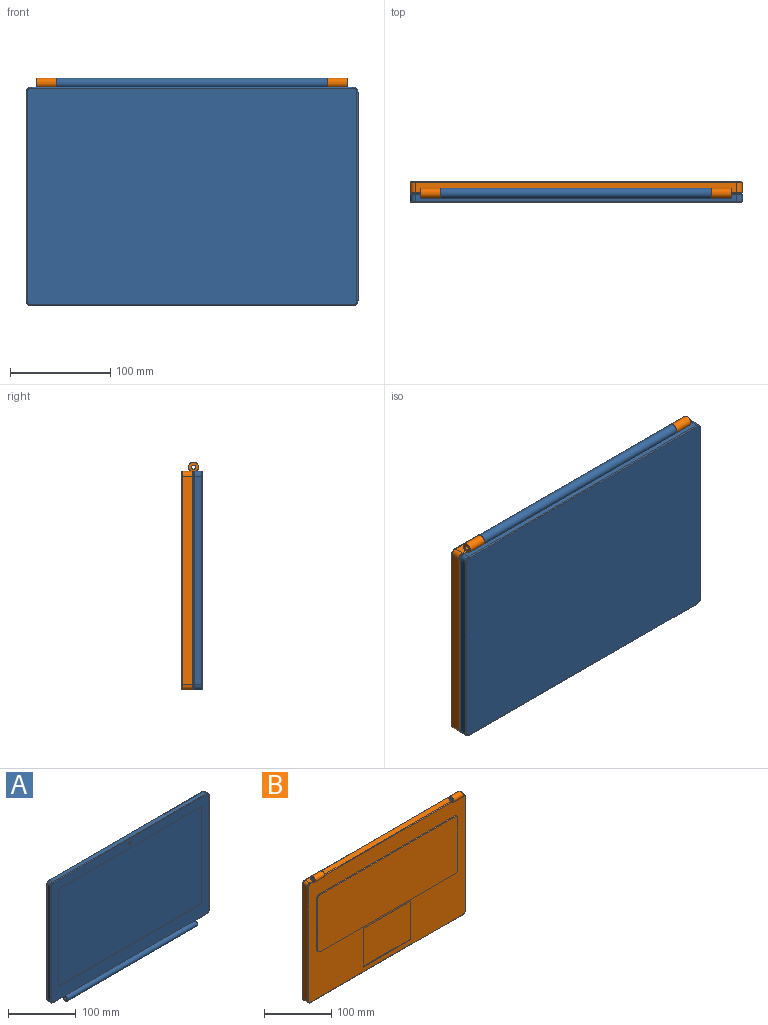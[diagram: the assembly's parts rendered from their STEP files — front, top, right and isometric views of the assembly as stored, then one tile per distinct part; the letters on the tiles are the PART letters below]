
ASSEMBLY  parts=2 mates=1
PART A: 38 faces, bbox 331.8x14x227.4 mm
  f0: plane 208x7mm, normal (-1,0,0), area 1456mm2, adj f17,f20,f23,f30
  f1: plane 321x7mm, normal (0,0,-1), area 1705mm2, adj f13,f14,f15,f17,f18,f21,f29,f34
  f2: plane 208x7mm, normal (1,0,0), area 1456mm2, adj f18,f19,f27,f37
  f3: plane 321x7mm, normal (0,0,1), area 2247mm2, adj f19,f20,f25,f33
  f4: plane 329x216mm, normal (0,-1,0), area 18398mm2, adj f6,f7,f8,f9,f11,f13,f21,f22
  f5: plane 329x216mm, normal (0,1,0), area 71050.3mm2, adj f30,f31,f32,f33,f34,f35,f36,f37
  f6: plane 176x1mm, normal (1,0,0), area 176mm2, adj f4,f7,f9,f10
  f7: plane 299x1mm, normal (0,0,1), area 299mm2, adj f4,f6,f8,f10
  f8: plane 176x1mm, normal (-1,0,0), area 176mm2, adj f4,f7,f9,f10
  f9: plane 299x1mm, normal (0,0,-1), area 299mm2, adj f4,f6,f8,f10
  f10: plane 299x176mm, normal (0,-1,0), area 52624mm2, adj f6,f7,f8,f9
  f11: cylinder r=3mm len=6mm, axis (0,-1,0), area 37.7mm2, adj f4,f12
  f12: plane 6x6mm, normal (0,-1,0), area 28.3mm2, adj f11
  f13: cylinder r=5mm len=271mm, axis (-1,0,0), area 7641.8mm2, adj f1,f4,f14,f15
  f14: plane 10x10mm, normal (1,0,0), area 64.1mm2, adj f1,f13,f16,f29
  f15: plane 10x10mm, normal (-1,0,0), area 64.1mm2, adj f1,f13,f16,f21
  f16: cylinder r=2mm len=271mm, axis (-1,0,0), area 3405.5mm2, adj f14,f15
  f17: cylinder r=5mm len=7mm, axis (0,1,0), area 55mm2, adj f0,f1,f22,f32
  f18: cylinder r=5mm len=7mm, axis (0,-1,0), area 55mm2, adj f1,f2,f28,f36
  f19: cylinder r=5mm len=7mm, axis (0,1,0), area 55mm2, adj f2,f3,f26,f35
  f20: cylinder r=5mm len=7mm, axis (0,-1,0), area 55mm2, adj f0,f3,f24,f31
  f21: cylinder r=1mm len=25mm, axis (-1,0,0), area 39.3mm2, adj f1,f4,f15,f22
  f22: torus R=4mm, axis (0,-1,0), area 11.4mm2, adj f4,f17,f21,f23
  f23: cylinder r=1mm len=208mm, axis (0,0,1), area 326.7mm2, adj f0,f4,f22,f24
  f24: torus R=4mm, axis (0,-1,0), area 11.4mm2, adj f4,f20,f23,f25
  f25: cylinder r=1mm len=321mm, axis (1,0,0), area 504.2mm2, adj f3,f4,f24,f26
  f26: torus R=4mm, axis (0,-1,0), area 11.4mm2, adj f4,f19,f25,f27
  f27: cylinder r=1mm len=208mm, axis (0,0,-1), area 326.7mm2, adj f2,f4,f26,f28
  f28: torus R=4mm, axis (0,-1,0), area 11.4mm2, adj f4,f18,f27,f29
  f29: cylinder r=1mm len=25mm, axis (-1,0,0), area 39.3mm2, adj f1,f4,f14,f28
  f30: cylinder r=1mm len=208mm, axis (0,0,-1), area 326.7mm2, adj f0,f5,f31,f32
  f31: torus R=4mm, axis (0,-1,0), area 11.4mm2, adj f5,f20,f30,f33
  f32: torus R=4mm, axis (0,-1,0), area 11.4mm2, adj f5,f17,f30,f34
  f33: cylinder r=1mm len=321mm, axis (-1,0,0), area 504.2mm2, adj f3,f5,f31,f35
  f34: cylinder r=1mm len=321mm, axis (1,0,0), area 504.2mm2, adj f1,f5,f32,f36
  f35: torus R=4mm, axis (0,-1,0), area 11.4mm2, adj f5,f19,f33,f37
  f36: torus R=4mm, axis (0,-1,0), area 11.4mm2, adj f5,f18,f34,f37
  f37: cylinder r=1mm len=208mm, axis (0,0,1), area 326.7mm2, adj f2,f5,f35,f36
PART B: 50 faces, bbox 331.8x17x227.4 mm
  f0: plane 321x10mm, normal (0,0,1), area 3130mm2, adj f20,f22,f23,f24,f26,f27,f30,f31
  f1: plane 329x216mm, normal (0,-1,0), area 33495.7mm2, adj f6,f7,f8,f9,f11,f12,f13,f14
  f2: plane 208x10mm, normal (-1,0,0), area 2080mm2, adj f28,f31,f36,f47
  f3: plane 321x10mm, normal (0,0,-1), area 3210mm2, adj f28,f29,f40,f46
  f4: plane 208x10mm, normal (1,0,0), area 2080mm2, adj f29,f30,f37,f42
  f5: plane 329x216mm, normal (0,1,0), area 71050.3mm2, adj f41,f42,f43,f44,f45,f46,f47,f48
  f6: plane 94x2mm, normal (-1,0,0), area 188mm2, adj f1,f10,f11,f14
  f7: plane 284x2mm, normal (0,0,-1), area 568mm2, adj f1,f10,f11,f12
  f8: plane 94x2mm, normal (1,0,0), area 188mm2, adj f1,f10,f12,f13
  f9: plane 284x2mm, normal (0,0,1), area 568mm2, adj f1,f10,f13,f14
  f10: plane 294x104mm, normal (0,-1,0), area 30554.5mm2, adj f6,f7,f8,f9,f11,f12,f13,f14
  f11: cylinder r=5mm len=5mm, axis (0,1,0), area 15.7mm2, adj f1,f6,f7,f10
  f12: cylinder r=5mm len=5mm, axis (0,-1,0), area 15.7mm2, adj f1,f7,f8,f10
  f13: cylinder r=5mm len=5mm, axis (0,1,0), area 15.7mm2, adj f1,f8,f9,f10
  f14: cylinder r=5mm len=5mm, axis (0,-1,0), area 15.7mm2, adj f1,f6,f9,f10
  f15: plane 70x1mm, normal (1,0,0), area 70mm2, adj f1,f16,f18,f19
  f16: plane 100x1mm, normal (0,0,1), area 100mm2, adj f1,f15,f17,f19
  f17: plane 70x1mm, normal (-1,0,0), area 70mm2, adj f1,f16,f18,f19
  f18: plane 100x1mm, normal (0,0,-1), area 100mm2, adj f1,f15,f17,f19
  f19: plane 100x70mm, normal (0,-1,0), area 7000mm2, adj f15,f16,f17,f18
  f20: cylinder r=5mm len=20mm, axis (1,0,0), area 564mm2, adj f0,f1,f22,f23
  f21: cylinder r=2mm len=20mm, axis (1,0,0), area 251.3mm2, adj f22,f23
  f22: plane 10x10mm, normal (-1,0,0), area 64.1mm2, adj f0,f20,f21,f49
  f23: plane 10x10mm, normal (1,0,0), area 64.1mm2, adj f0,f20,f21,f33
  f24: cylinder r=5mm len=20mm, axis (-1,0,0), area 564mm2, adj f0,f1,f26,f27
  f25: cylinder r=2mm len=20mm, axis (-1,0,0), area 251.3mm2, adj f26,f27
  f26: plane 10x10mm, normal (1,0,0), area 64.1mm2, adj f0,f24,f25,f49
  f27: plane 10x10mm, normal (-1,0,0), area 64.1mm2, adj f0,f24,f25,f32
  f28: cylinder r=5mm len=10mm, axis (0,1,0), area 78.5mm2, adj f2,f3,f38,f48
  f29: cylinder r=5mm len=10mm, axis (0,-1,0), area 78.5mm2, adj f3,f4,f39,f44
  f30: cylinder r=5mm len=10mm, axis (0,1,0), area 78.5mm2, adj f0,f4,f35,f41
  f31: cylinder r=5mm len=10mm, axis (0,-1,0), area 78.5mm2, adj f0,f2,f34,f45
  f32: cylinder r=1mm len=5mm, axis (1,0,0), area 7.9mm2, adj f0,f1,f27,f34
  f33: cylinder r=1mm len=5mm, axis (1,0,0), area 7.9mm2, adj f0,f1,f23,f35
  f34: torus R=4mm, axis (0,-1,0), area 11.4mm2, adj f1,f31,f32,f36
  f35: torus R=4mm, axis (0,-1,0), area 11.4mm2, adj f1,f30,f33,f37
  f36: cylinder r=1mm len=208mm, axis (0,0,1), area 326.7mm2, adj f1,f2,f34,f38
  f37: cylinder r=1mm len=208mm, axis (0,0,-1), area 326.7mm2, adj f1,f4,f35,f39
  f38: torus R=4mm, axis (0,-1,0), area 11.4mm2, adj f1,f28,f36,f40
  f39: torus R=4mm, axis (0,-1,0), area 11.4mm2, adj f1,f29,f37,f40
  f40: cylinder r=1mm len=321mm, axis (-1,0,0), area 504.2mm2, adj f1,f3,f38,f39
  f41: torus R=4mm, axis (0,-1,0), area 11.4mm2, adj f5,f30,f42,f43
  f42: cylinder r=1mm len=208mm, axis (0,0,1), area 326.7mm2, adj f4,f5,f41,f44
  f43: cylinder r=1mm len=321mm, axis (-1,0,0), area 504.2mm2, adj f0,f5,f41,f45
  f44: torus R=4mm, axis (0,-1,0), area 11.4mm2, adj f5,f29,f42,f46
  f45: torus R=4mm, axis (0,-1,0), area 11.4mm2, adj f5,f31,f43,f47
  f46: cylinder r=1mm len=321mm, axis (1,0,0), area 504.2mm2, adj f3,f5,f44,f48
  f47: cylinder r=1mm len=208mm, axis (0,0,-1), area 326.7mm2, adj f2,f5,f45,f48
  f48: torus R=4mm, axis (0,-1,0), area 11.4mm2, adj f5,f28,f46,f47
  f49: cylinder r=1mm len=271mm, axis (1,0,0), area 425.7mm2, adj f0,f1,f22,f26
PLACE A rot(axis=(-1,0,0),180deg) t=(68.16,101.6,189.79)mm
PLACE B t=(68.16,122.6,-28.21)mm
MATE revolute B.f24 <-> A.f13  axis (1,0,0) through (-67.34,110.6,193.79)mm
